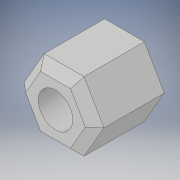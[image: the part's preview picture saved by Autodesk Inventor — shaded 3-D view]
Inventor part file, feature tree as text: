
AUTODESK INVENTOR PART (.ipt)
format: ipt  version: 2018 (Build 220112000, 112)  size: 107,008 bytes
history: native  units: in
note: dims shown in document units (in); Inventor stores cm internally (conversion verified against a paired STEP export)
features: extrude x1, chamfer x1, sketch x1
ambient origin geometry x8: Origin, YZ Plane, XZ Plane, XY Plane, X Axis, Y Axis, Z Axis, Center Point
bodies: Solid1 (feature_tree)
feature tree (3):
  extrude  "Extrusion1"  Depth=0.125in
  chamfer  "Chamfer1"  Distance=0.5in
  sketch  "Sketch1"  dims[d0=0.5in d1=0.25in d2=0.5in d3=0.0in d4=0.0625in d5=0.125in d6=45.0deg]
